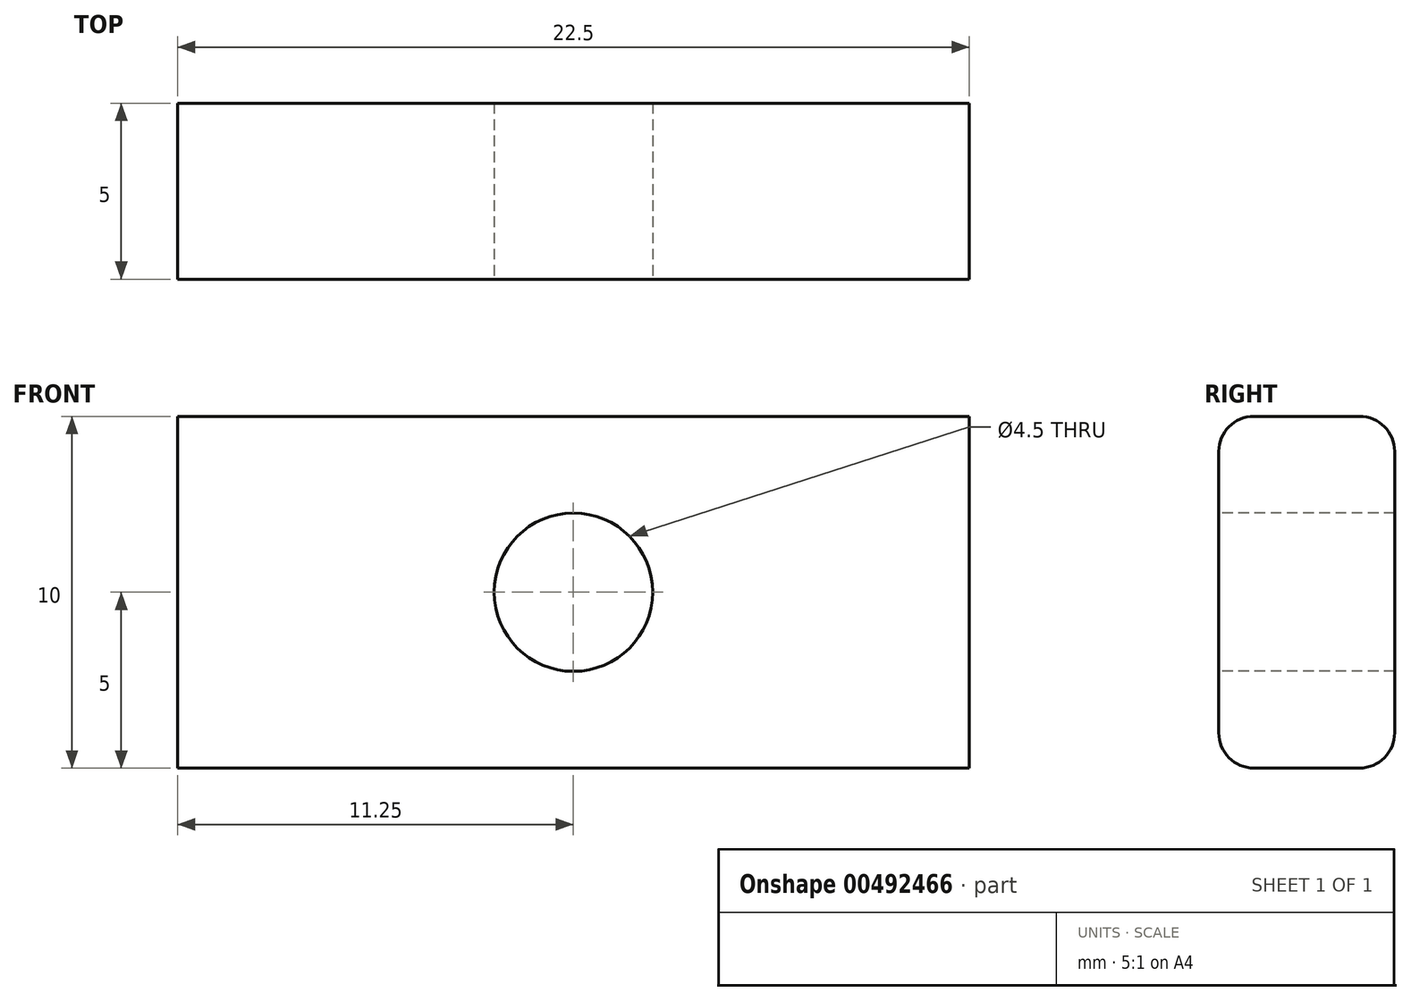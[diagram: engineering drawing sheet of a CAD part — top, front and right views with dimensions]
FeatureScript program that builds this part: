
annotation { "Feature Type Name" : "Feature", "Feature Type Description" : "" }
export const myFeature = defineFeature(function(context is Context, id is Id, definition is map)
    precondition{}
    {
        {
            var Q0;
            Q0=qCreatedBy(makeId("Right.planeOp"),FACE);
            var sketch = newSketch(context, id + "F0", { "sketchPlane" : qUnion([Q0])});
            skLineSegment(sketch, "E0", {"start": v(0, 5) * mm, "end": v(0, -5) * mm});
            skLineSegment(sketch, "E1", {"start": v(-0.96, 0) * mm, "end": v(5.8, 0) * mm, "construction": true});
            skLineSegment(sketch, "E2", {"start": v(5, 5) * mm, "end": v(0, 5) * mm});
            skLineSegment(sketch, "E3", {"start": v(5, -5) * mm, "end": v(0, -5) * mm});
            skLineSegment(sketch, "E4", {"start": v(5, 5) * mm, "end": v(5, -5) * mm});
            skSolve(sketch);
        }
        {
            var Q0;
            Q0 = qSketchRegion(id + "F0", true);
            extrude(context, id + "F1", {"entities" : qUnion([Q0]), "depth" : 22.5 * mm, "offsetDistance" : 25 * mm, "symmetric" : true});
        }
        {
            var Q0;
            Q0=makeQuery(id+"F1.opExtrude","SWEPT_FACE",FACE,{"disambiguationData":[OSD([sQuery(id+"F0.wireOp",EDGE,"E0")])]});
            var sketch = newSketch(context, id + "F2", { "sketchPlane" : qUnion([Q0])});
            skCircle(sketch, "E5", {"center": v(0, 0) * mm, "radius": 2.25 * mm});
            skPoint(sketch, "E5.centerSnap0", {"position": v(-11.25, 0) * mm});
            skSolve(sketch);
        }
        {
            var Q0;
            Q0 = qSketchRegion(id + "F2", true);
            extrude(context, id + "F3", {"entities" : qUnion([Q0]), "operationType" : NewBodyOperationType.REMOVE, "endBound" : BoundingType.THROUGH_ALL, "oppositeDirection" : true, "depth" : 25 * mm, "offsetDistance" : 25 * mm});
        }
        {
            var Q0;
            Q0=makeQuery(id+"F1.opExtrude","SWEPT_EDGE",EDGE,{"disambiguationData":[OSD([sQuery(id+"F0.wireOp",EDGE,"E0"),sQuery(id+"F0.wireOp",EDGE,"E2")])]});
            var Q1;
            Q1=makeQuery(id+"F1.opExtrude","SWEPT_EDGE",EDGE,{"disambiguationData":[OSD([sQuery(id+"F0.wireOp",EDGE,"E0"),sQuery(id+"F0.wireOp",EDGE,"E3")])]});
            var Q2;
            Q2=makeQuery(id+"F1.opExtrude","SWEPT_EDGE",EDGE,{"disambiguationData":[OSD([sQuery(id+"F0.wireOp",EDGE,"E2"),sQuery(id+"F0.wireOp",EDGE,"E4")])]});
            var Q3;
            Q3=makeQuery(id+"F1.opExtrude","SWEPT_EDGE",EDGE,{"disambiguationData":[OSD([sQuery(id+"F0.wireOp",EDGE,"E3"),sQuery(id+"F0.wireOp",EDGE,"Y59T1LJf-PLBk-j0Wz-z3nx-ODQuLbRXI5gn")])]});
            fillet(context, id + "F4", {"entities" : qUnion([Q0, Q1, Q2, Q3]), "radius" : 1 * mm, "tangentPropagation" : true, "allowEdgeOverflow" : false});
        }
    });
